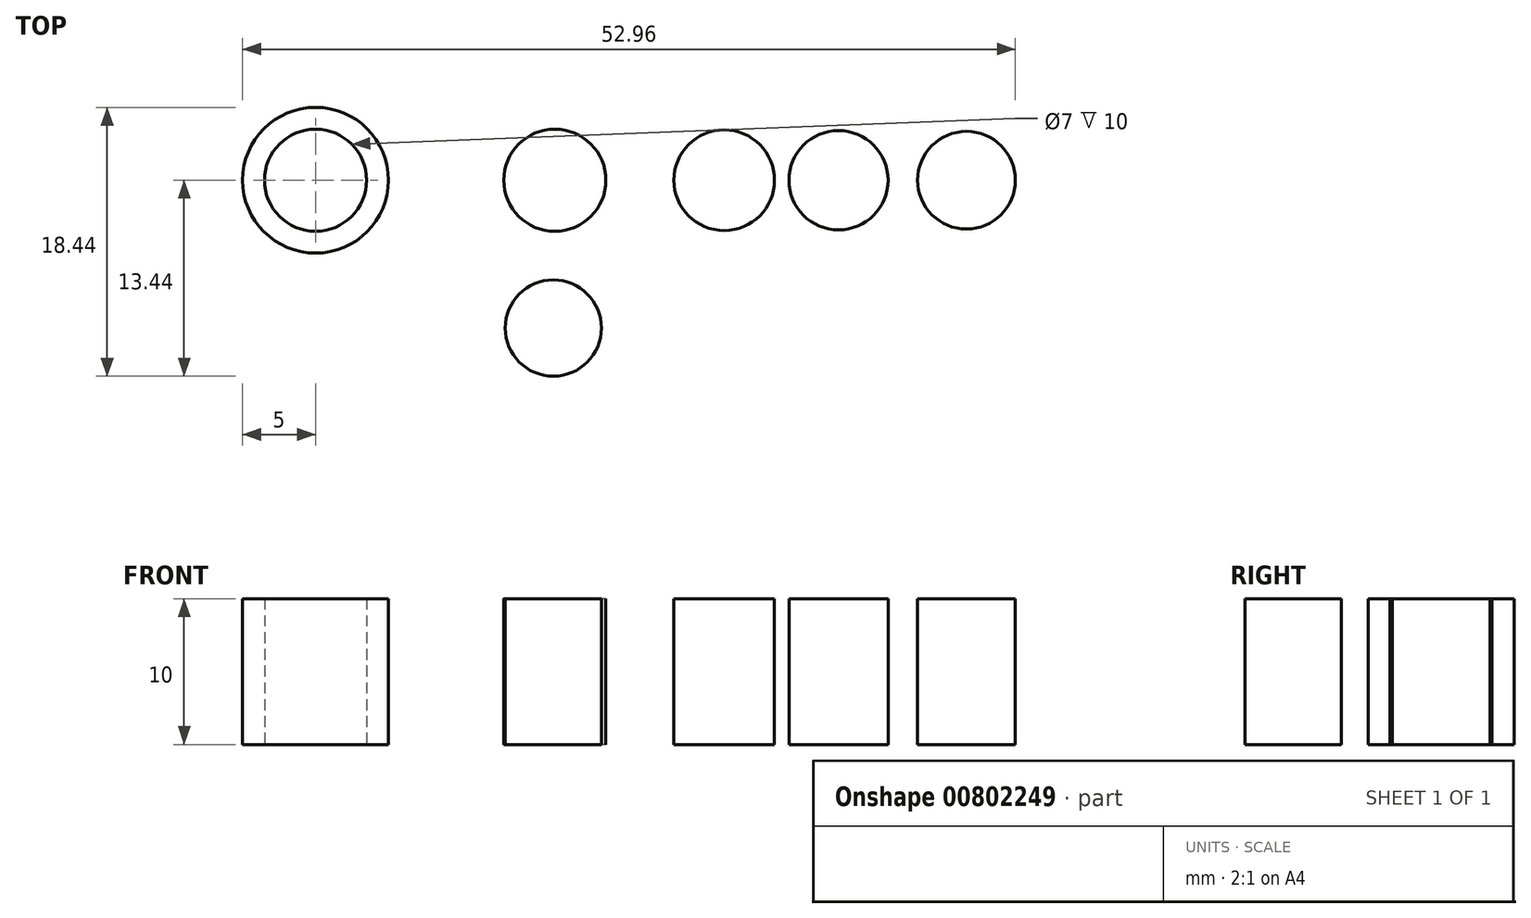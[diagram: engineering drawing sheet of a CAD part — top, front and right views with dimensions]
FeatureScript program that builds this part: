
annotation { "Feature Type Name" : "Feature", "Feature Type Description" : "" }
export const myFeature = defineFeature(function(context is Context, id is Id, definition is map)
    precondition{}
    {
        {
            var Q0;
            Q0=qCreatedBy(makeId("Top.planeOp"),FACE);
            var sketch = newSketch(context, id + "F0", { "sketchPlane" : qUnion([Q0])});
            skCircle(sketch, "E0", {"center": v(0, 0) * mm, "radius": 3.5 * mm});
            skCircle(sketch, "E1", {"center": v(0, 0) * mm, "radius": 5 * mm});
            skCircle(sketch, "E2", {"center": v(16.4, 0) * mm, "radius": 3.5 * mm});
            skCircle(sketch, "E3", {"center": v(28, 0) * mm, "radius": 3.45 * mm});
            skCircle(sketch, "E4", {"center": v(35.84, 0) * mm, "radius": 3.4 * mm});
            skCircle(sketch, "E5", {"center": v(44.61, 0) * mm, "radius": 3.35 * mm});
            skCircle(sketch, "E6", {"center": v(16.3, -10.14) * mm, "radius": 3.3 * mm});
            skSolve(sketch);
        }
        {
            var Q0;
            Q0=makeQuery(id+"F0.imprint","IMPRINT",FACE,{"disambiguationData":[TD([[makeQuery(id+"F0.imprint","IMPRINT",EDGE,{"derivedFrom":sQuery(id+"F0.wireOp",EDGE,"E0")}),-1.0]])]});
            var Q1;
            Q1=makeQuery(id+"F0.imprint","IMPRINT",FACE,{"disambiguationData":[TD([[makeQuery(id+"F0.imprint","IMPRINT",EDGE,{"derivedFrom":sQuery(id+"F0.wireOp",EDGE,"E2")}),1.0]])]});
            var Q2;
            Q2=makeQuery(id+"F0.imprint","IMPRINT",FACE,{"disambiguationData":[TD([[makeQuery(id+"F0.imprint","IMPRINT",EDGE,{"derivedFrom":sQuery(id+"F0.wireOp",EDGE,"E3")}),1.0]])]});
            var Q3;
            Q3=makeQuery(id+"F0.imprint","IMPRINT",FACE,{"disambiguationData":[TD([[makeQuery(id+"F0.imprint","IMPRINT",EDGE,{"derivedFrom":sQuery(id+"F0.wireOp",EDGE,"E4")}),1.0]])]});
            var Q4;
            Q4=makeQuery(id+"F0.imprint","IMPRINT",FACE,{"disambiguationData":[TD([[makeQuery(id+"F0.imprint","IMPRINT",EDGE,{"derivedFrom":sQuery(id+"F0.wireOp",EDGE,"E5")}),1.0]])]});
            var Q5;
            Q5=makeQuery(id+"F0.imprint","IMPRINT",FACE,{"disambiguationData":[TD([[makeQuery(id+"F0.imprint","IMPRINT",EDGE,{"derivedFrom":sQuery(id+"F0.wireOp",EDGE,"E6")}),1.0]])]});
            extrude(context, id + "F1", {"entities" : qUnion([Q0, Q1, Q2, Q3, Q4, Q5]), "depth" : 10 * mm, "offsetDistance" : 25 * mm});
        }
    });
